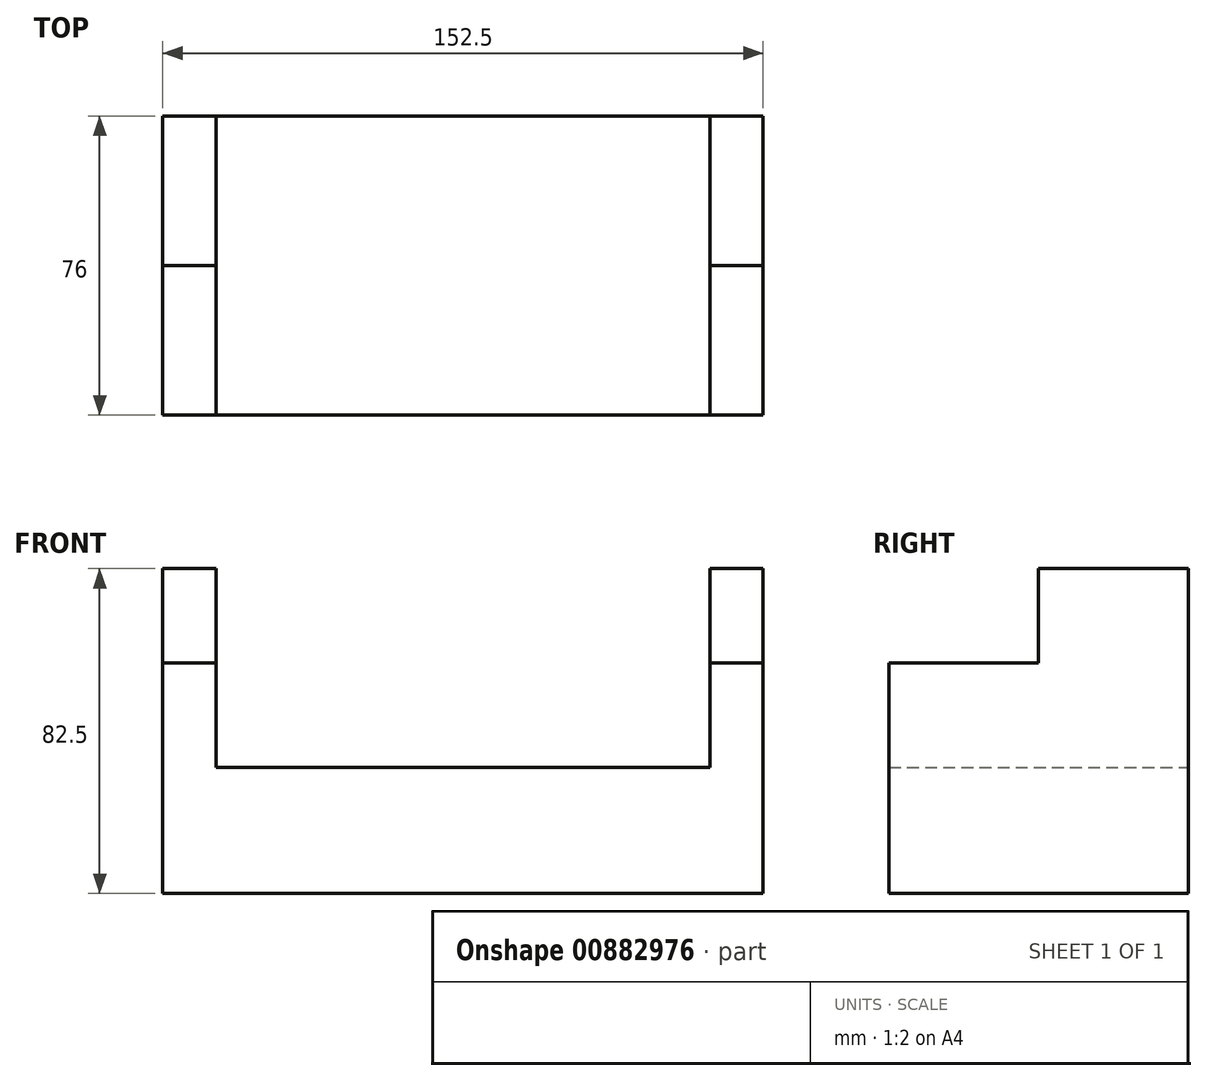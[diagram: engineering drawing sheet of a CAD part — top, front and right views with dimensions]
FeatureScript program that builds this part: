
annotation { "Feature Type Name" : "Feature", "Feature Type Description" : "" }
export const myFeature = defineFeature(function(context is Context, id is Id, definition is map)
    precondition{}
    {
        {
            var Q0;
            Q0=qCreatedBy(makeId("Front.planeOp"),FACE);
            var sketch = newSketch(context, id + "F0", { "sketchPlane" : qUnion([Q0])});
            skLineSegment(sketch, "E0", {"start": v(0, 0) * mm, "end": v(-152.5, 0) * mm});
            skLineSegment(sketch, "E1", {"start": v(-152.5, 0) * mm, "end": v(-152.5, 82.5) * mm});
            skLineSegment(sketch, "E2", {"start": v(-152.5, 82.5) * mm, "end": v(-139, 82.5) * mm});
            skLineSegment(sketch, "E3", {"start": v(-139, 82.5) * mm, "end": v(-139, 32) * mm});
            skLineSegment(sketch, "E4", {"start": v(-139, 32) * mm, "end": v(-13.5, 32) * mm});
            skLineSegment(sketch, "E5", {"start": v(-13.5, 32) * mm, "end": v(-13.5, 82.5) * mm});
            skLineSegment(sketch, "E6", {"start": v(-13.5, 82.5) * mm, "end": v(0, 82.5) * mm});
            skLineSegment(sketch, "E7", {"start": v(0, 82.5) * mm, "end": v(0, 0) * mm});
            skSolve(sketch);
        }
        {
            var Q0;
            Q0=makeQuery(id+"F0.imprint","IMPRINT",FACE,{"disambiguationData":[TD([[makeQuery(id+"F0.imprint","IMPRINT",EDGE,{"derivedFrom":sQuery(id+"F0.wireOp",EDGE,"E0")}),-1.0]])]});
            extrude(context, id + "F1", {"entities" : qUnion([Q0]), "depth" : 38 * mm, "offsetDistance" : 25 * mm});
        }
        {
            var Q0;
            Q0=makeQuery(id+"F1.opExtrude","CAP_FACE",FACE,{"disambiguationData":[OSD([sQuery(id+"F0.wireOp",EDGE,"E0"),sQuery(id+"F0.wireOp",EDGE,"E1"),sQuery(id+"F0.wireOp",EDGE,"E2"),sQuery(id+"F0.wireOp",EDGE,"E3"),sQuery(id+"F0.wireOp",EDGE,"E4"),sQuery(id+"F0.wireOp",EDGE,"E5"),sQuery(id+"F0.wireOp",EDGE,"E6"),sQuery(id+"F0.wireOp",EDGE,"E7")])],"isStart":false});
            var sketch = newSketch(context, id + "F2", { "sketchPlane" : qUnion([Q0])});
            skLineSegment(sketch, "E8", {"start": v(-152.5, 0) * mm, "end": v(-152.5, 58.5) * mm});
            skLineSegment(sketch, "E9", {"start": v(-152.5, 58.5) * mm, "end": v(-139, 58.5) * mm});
            skLineSegment(sketch, "E10", {"start": v(-139, 58.5) * mm, "end": v(-139, 32) * mm});
            skLineSegment(sketch, "E11", {"start": v(-139, 32) * mm, "end": v(-13.5, 32) * mm});
            skLineSegment(sketch, "E12", {"start": v(-13.5, 32) * mm, "end": v(-13.5, 58.5) * mm});
            skLineSegment(sketch, "E13", {"start": v(-13.5, 58.5) * mm, "end": v(0, 58.5) * mm});
            skLineSegment(sketch, "E14", {"start": v(0, 58.5) * mm, "end": v(0, 0) * mm});
            skLineSegment(sketch, "E15", {"start": v(0, 0) * mm, "end": v(-152.5, 0) * mm});
            skSolve(sketch);
        }
        {
            var Q0;
            Q0=makeQuery(id+"F2.imprint","IMPRINT",FACE,{"disambiguationData":[TD([[makeQuery(id+"F2.imprint","IMPRINT",EDGE,{"derivedFrom":sQuery(id+"F2.wireOp",EDGE,"E8")}),-1.0]])]});
            extrude(context, id + "F3", {"entities" : qUnion([Q0]), "operationType" : NewBodyOperationType.ADD, "depth" : 38 * mm, "offsetDistance" : 25 * mm});
        }
    });
